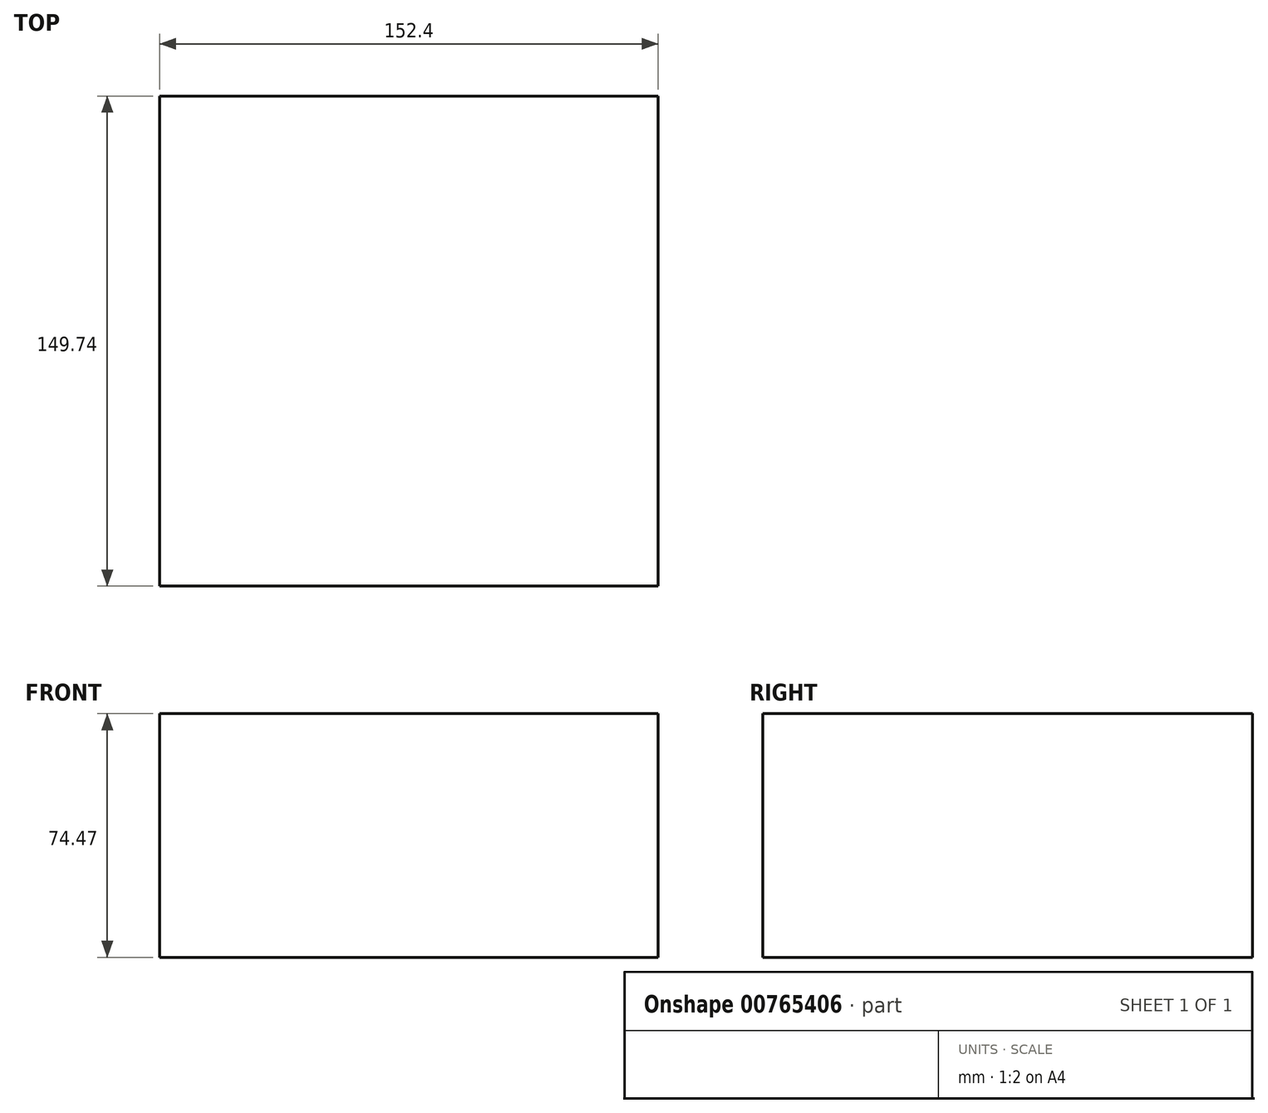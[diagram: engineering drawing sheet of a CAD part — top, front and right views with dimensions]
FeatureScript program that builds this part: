
annotation { "Feature Type Name" : "Feature", "Feature Type Description" : "" }
export const myFeature = defineFeature(function(context is Context, id is Id, definition is map)
    precondition{}
    {
        {
            var Q0;
            Q0=qCreatedBy(makeId("Right.planeOp"),FACE);
            var sketch = newSketch(context, id + "F0", { "sketchPlane" : qUnion([Q0])});
            skLineSegment(sketch, "E0", {"start": v(0, 0) * mm, "end": v(0, 74.47) * mm});
            skLineSegment(sketch, "E1", {"start": v(0, 74.47) * mm, "end": v(74.33, 74.47) * mm});
            skLineSegment(sketch, "E2", {"start": v(74.33, 74.47) * mm, "end": v(74.33, 0) * mm});
            skLineSegment(sketch, "E3", {"start": v(74.33, 0) * mm, "end": v(0, 0) * mm});
            skLineSegment(sketch, "E4", {"start": v(0, 0) * mm, "end": v(-75.4, 0) * mm});
            skLineSegment(sketch, "E5", {"start": v(-75.4, 0) * mm, "end": v(-75.4, 74.47) * mm});
            skLineSegment(sketch, "E6", {"start": v(-75.4, 74.47) * mm, "end": v(0, 74.47) * mm});
            skLineSegment(sketch, "E7", {"start": v(0, 74.47) * mm, "end": v(0, 0) * mm});
            skSolve(sketch);
        }
        {
            var Q0;
            Q0=makeQuery(id+"F0.imprint","IMPRINT",FACE,{"disambiguationData":[TD([[makeQuery(id+"F0.imprint","IMPRINT",EDGE,{"derivedFrom":sQuery(id+"F0.wireOp",EDGE,"E4")}),-1.0]])]});
            var Q1;
            Q1=makeQuery(id+"F0.imprint","IMPRINT",FACE,{"disambiguationData":[TD([[makeQuery(id+"F0.imprint","IMPRINT",EDGE,{"derivedFrom":sQuery(id+"F0.wireOp",EDGE,"E1")}),-1.0]])]});
            extrude(context, id + "F1", {"entities" : qUnion([Q0, Q1]), "depth" : 76.2 * mm, "offsetDistance" : 25.4 * mm});
        }
        {
            var Q0;
            Q0=makeQuery(id+"F1.opExtrude","CAP_FACE",FACE,{"disambiguationData":[OSD([sQuery(id+"F0.wireOp",EDGE,"E1"),sQuery(id+"F0.wireOp",EDGE,"E2"),sQuery(id+"F0.wireOp",EDGE,"E3"),sQuery(id+"F0.wireOp",EDGE,"E4"),sQuery(id+"F0.wireOp",EDGE,"E5"),sQuery(id+"F0.wireOp",EDGE,"E6")])],"isStart":true});
            extrude(context, id + "F2", {"entities" : qUnion([Q0]), "operationType" : NewBodyOperationType.ADD, "depth" : 76.2 * mm, "offsetDistance" : 25.4 * mm});
        }
    });
